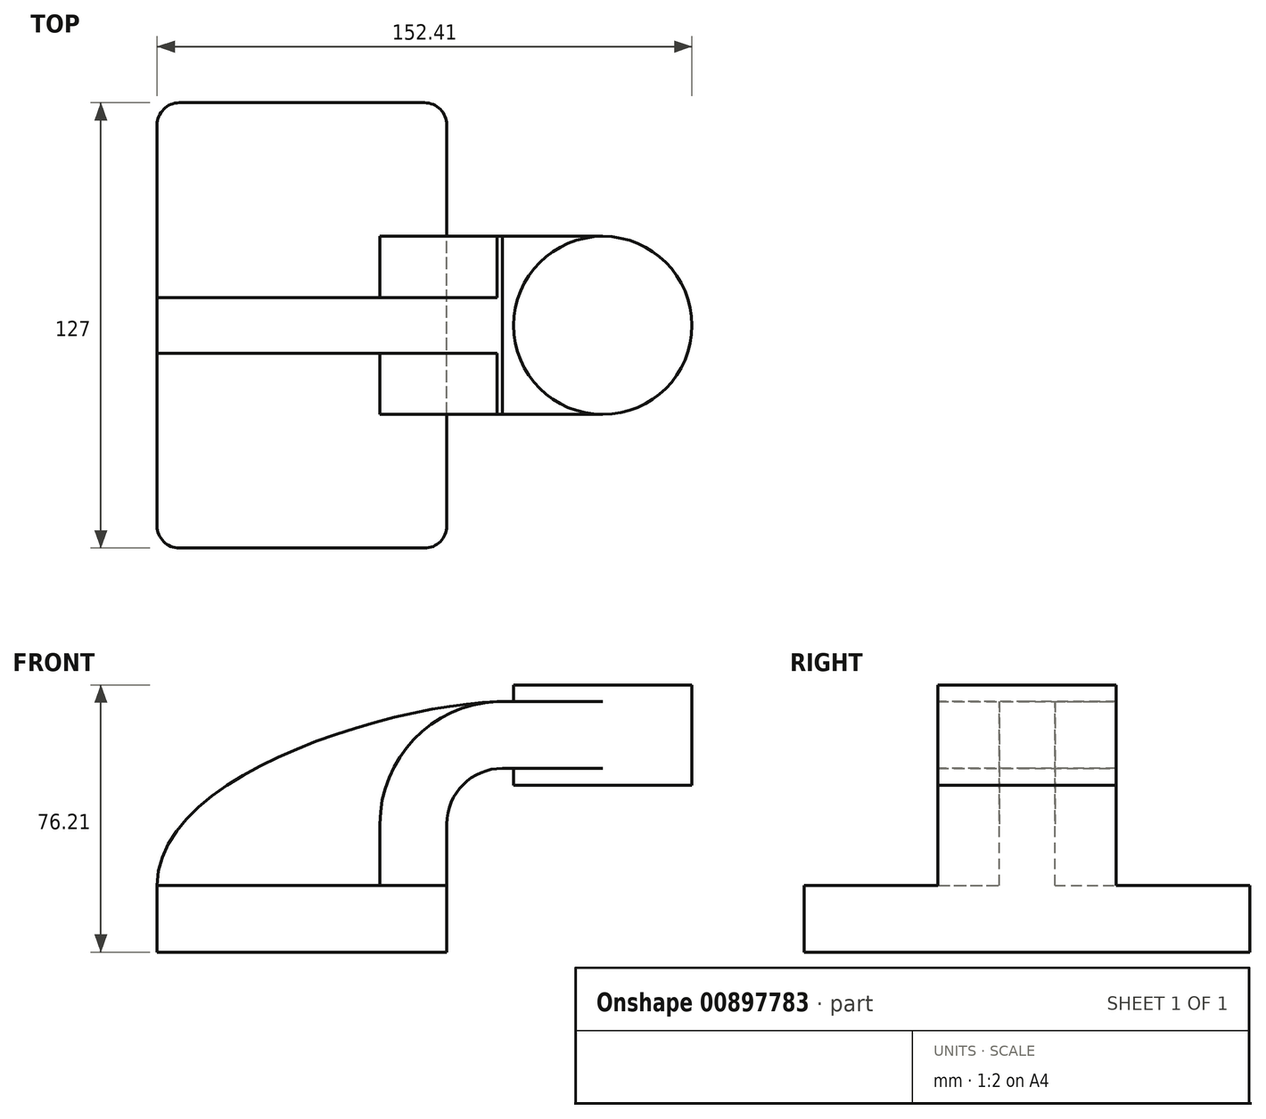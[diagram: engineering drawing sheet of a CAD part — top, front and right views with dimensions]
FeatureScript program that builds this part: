
annotation { "Feature Type Name" : "Feature", "Feature Type Description" : "" }
export const myFeature = defineFeature(function(context is Context, id is Id, definition is map)
    precondition{}
    {
        {
            var Q0;
            Q0=qCreatedBy(makeId("Front.planeOp"),FACE);
            var sketch = newSketch(context, id + "F0", { "sketchPlane" : qUnion([Q0])});
            skLineSegment(sketch, "E0.bottom", {"start": v(41.28, -9.52) * mm, "end": v(-41.27, -9.53) * mm});
            skLineSegment(sketch, "E0.top", {"start": v(41.27, 9.53) * mm, "end": v(-41.27, 9.53) * mm});
            skLineSegment(sketch, "E0.left", {"start": v(41.28, -9.52) * mm, "end": v(41.28, 9.53) * mm});
            skLineSegment(sketch, "E0.right", {"start": v(-41.27, -9.53) * mm, "end": v(-41.27, 9.53) * mm});
            skPoint(sketch, "E0.middle", {"position": v(0, 0) * mm});
            skLineSegment(sketch, "E1.bottom", {"start": v(111.12, 38.1) * mm, "end": v(60.32, 38.1) * mm});
            skLineSegment(sketch, "E1.top", {"start": v(111.12, 66.68) * mm, "end": v(60.32, 66.68) * mm});
            skLineSegment(sketch, "E1.left", {"start": v(111.12, 38.1) * mm, "end": v(111.12, 66.68) * mm});
            skLineSegment(sketch, "E1.right", {"start": v(60.32, 38.1) * mm, "end": v(60.32, 66.68) * mm});
            skPoint(sketch, "E1.middle", {"position": v(85.72, 52.39) * mm});
            skLineSegment(sketch, "E2", {"start": v(41.27, 9.53) * mm, "end": v(41.27, 27) * mm});
            skArc(sketch, "E3", {"start": v(41.27, 27) * mm, "mid": v(45.92, 38.23) * mm, "end": v(57.15, 42.88) * mm});
            skLineSegment(sketch, "E4", {"start": v(57.15, 42.88) * mm, "end": v(85.72, 42.88) * mm});
            skLineSegment(sketch, "E5.0", {"start": v(57.15, 61.93) * mm, "end": v(85.72, 61.93) * mm});
            skArc(sketch, "E5.1", {"start": v(22.22, 27) * mm, "mid": v(32.45, 51.7) * mm, "end": v(57.15, 61.93) * mm});
            skLineSegment(sketch, "E5.2", {"start": v(22.22, 9.53) * mm, "end": v(22.22, 27) * mm});
            skLineSegment(sketch, "E6", {"start": v(85.72, 38.1) * mm, "end": v(85.72, 66.68) * mm});
            skFitSpline(sketch, "E7", {"points": [v(-41.28, 9.52) * mm, v(57.15, 61.93) * mm], "startDerivative": vector(0.04, 97.08) * mm, "endDerivative": vector(87.93, 1.04) * mm});
            skSolve(sketch);
        }
        {
            var Q0;
            Q0=makeQuery(id+"F0.imprint","IMPRINT",FACE,{"disambiguationData":[TD([[makeQuery(id+"F0.imprint","IMPRINT",EDGE,{"derivedFrom":sQuery(id+"F0.wireOp",EDGE,"E0.bottom")}),-1.0]])]});
            extrude(context, id + "F1", {"entities" : qUnion([Q0]), "depth" : 127 * mm, "offsetDistance" : 25.4 * mm, "symmetric" : true});
        }
        {
            var Q0;
            {var subQ1=sQuery(id+"F0.wireOp",EDGE,"E2");Q0=makeQuery(id+"F0.imprint","IMPRINT",FACE,{"disambiguationData":[TD([[makeQuery(id+"F0.imprint","IMPRINT",EDGE,{"derivedFrom":subQ1}),1.0]])]});}
            var Q1;
            {var subQ0=sQuery(id+"F0.wireOp",EDGE,"E4");var subQ1=sQuery(id+"F0.wireOp",EDGE,"E1.right");var subQ2=makeQuery(id+"F0.imprint","INTERSECT",VERTEX,{"derivedFrom":[subQ1,subQ0]});Q1=makeQuery(id+"F0.imprint","IMPRINT",FACE,{"disambiguationData":[TD([[makeQuery(id+"F0.imprint","IMPRINT",EDGE,{"disambiguationData":[TD([[subQ2,-1.0]])],"derivedFrom":subQ1}),-1.0]])]});}
            extrude(context, id + "F2", {"entities" : qUnion([Q0, Q1]), "operationType" : NewBodyOperationType.ADD, "depth" : 50.8 * mm, "offsetDistance" : 25.4 * mm, "symmetric" : true});
        }
        {
            var Q0;
            {var subQ3=sQuery(id+"F0.wireOp",EDGE,"E5.2");Q0=makeQuery(id+"F0.imprint","IMPRINT",FACE,{"disambiguationData":[TD([[makeQuery(id+"F0.imprint","IMPRINT",EDGE,{"derivedFrom":subQ3}),1.0]])]});}
            extrude(context, id + "F3", {"entities" : qUnion([Q0]), "operationType" : NewBodyOperationType.ADD, "depth" : 15.88 * mm, "offsetDistance" : 25.4 * mm, "symmetric" : true});
        }
        {
            var Q0;
            {var subQ0=sQuery(id+"F0.wireOp",EDGE,"E1.left");Q0=makeQuery(id+"F0.imprint","IMPRINT",FACE,{"disambiguationData":[TD([[makeQuery(id+"F0.imprint","IMPRINT",EDGE,{"derivedFrom":subQ0}),1.0]])]});}
            var Q1;
            Q1=sQuery(id+"F0.wireOp",EDGE,"E6");
            revolve(context, id + "F4", {"operationType" : NewBodyOperationType.ADD, "surfaceOperationType" : NewSurfaceOperationType.NEW, "entities" : qUnion([Q0]), "axis" : qUnion([Q1]), "revolveType" : RevolveType.FULL});
        }
        {
            var Q0;
            Q0=makeQuery(id+"F1.opExtrude","CAP_EDGE",EDGE,{"disambiguationData":[OSD([sQuery(id+"F0.wireOp",EDGE,"E0.right")])],"isStart":false});
            var Q1;
            Q1=makeQuery(id+"F1.opExtrude","CAP_EDGE",EDGE,{"disambiguationData":[OSD([sQuery(id+"F0.wireOp",EDGE,"E0.left")])],"isStart":false});
            var Q2;
            Q2=makeQuery(id+"F1.opExtrude","CAP_EDGE",EDGE,{"disambiguationData":[OSD([sQuery(id+"F0.wireOp",EDGE,"E0.left")])],"isStart":true});
            var Q3;
            Q3=makeQuery(id+"F1.opExtrude","CAP_EDGE",EDGE,{"disambiguationData":[OSD([sQuery(id+"F0.wireOp",EDGE,"E0.right")])],"isStart":true});
            fillet(context, id + "F5", {"entities" : qUnion([Q0, Q1, Q2, Q3]), "radius" : 6.35 * mm, "tangentPropagation" : true, "allowEdgeOverflow" : false});
        }
    });
